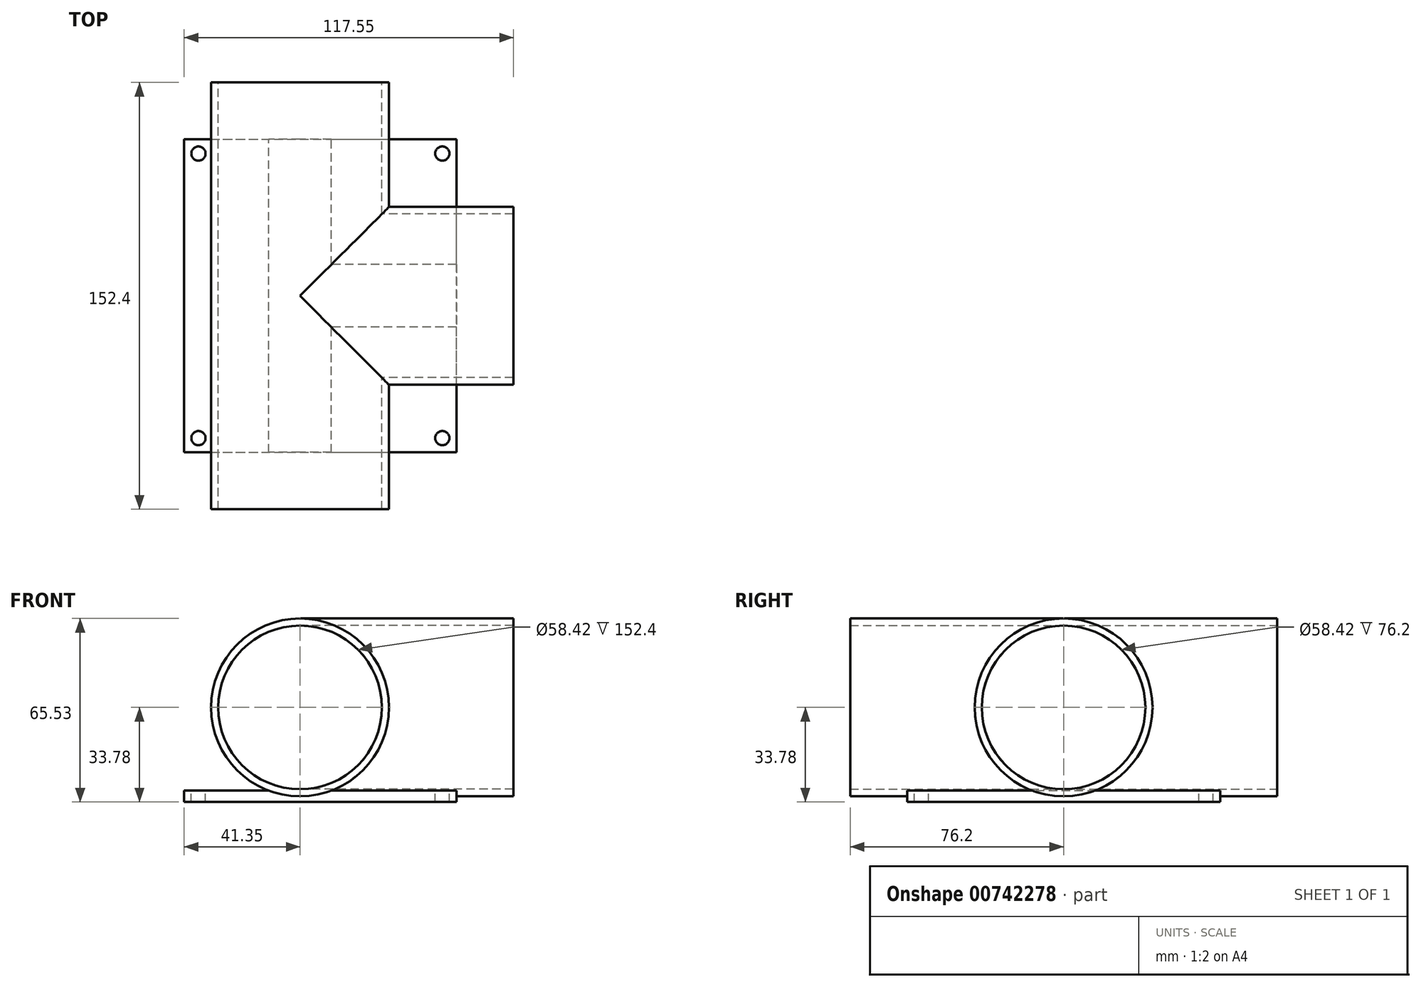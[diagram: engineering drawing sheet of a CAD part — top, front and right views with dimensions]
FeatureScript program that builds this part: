
annotation { "Feature Type Name" : "Feature", "Feature Type Description" : "" }
export const myFeature = defineFeature(function(context is Context, id is Id, definition is map)
    precondition{}
    {
        {
            var Q0;
            Q0=qCreatedBy(makeId("Front.planeOp"),FACE);
            var sketch = newSketch(context, id + "F0", { "sketchPlane" : qUnion([Q0])});
            skCircle(sketch, "E0", {"center": v(0, 0) * mm, "radius": 31.75 * mm});
            skCircle(sketch, "E1.0", {"center": v(0, 0) * mm, "radius": 29.21 * mm});
            skSolve(sketch);
        }
        {
            var Q0;
            Q0=makeQuery(id+"F0.imprint","IMPRINT",FACE,{"disambiguationData":[TD([[makeQuery(id+"F0.imprint","IMPRINT",EDGE,{"derivedFrom":sQuery(id+"F0.wireOp",EDGE,"E0")}),1.0]])]});
            extrude(context, id + "F1", {"entities" : qUnion([Q0]), "endBound" : BoundingType.SYMMETRIC, "depth" : 152.4 * mm, "offsetDistance" : 25.4 * mm});
        }
        {
            var Q0;
            Q0=qCreatedBy(makeId("Right.planeOp"),FACE);
            var sketch = newSketch(context, id + "F2", { "sketchPlane" : qUnion([Q0])});
            skCircle(sketch, "E2", {"center": v(0, 0) * mm, "radius": 31.75 * mm});
            skCircle(sketch, "E3.0", {"center": v(0, 0) * mm, "radius": 29.21 * mm});
            skSolve(sketch);
        }
        {
            var Q0;
            Q0=makeQuery(id+"F2.imprint","IMPRINT",FACE,{"disambiguationData":[TD([[makeQuery(id+"F2.imprint","IMPRINT",EDGE,{"derivedFrom":sQuery(id+"F2.wireOp",EDGE,"E2")}),1.0]])]});
            extrude(context, id + "F3", {"entities" : qUnion([Q0]), "operationType" : NewBodyOperationType.ADD, "depth" : 76.2 * mm, "offsetDistance" : 25.4 * mm});
        }
        {
            var Q0;
            Q0=makeQuery(id+"F0.imprint","IMPRINT",FACE,{"disambiguationData":[TD([[makeQuery(id+"F0.imprint","IMPRINT",EDGE,{"derivedFrom":sQuery(id+"F0.wireOp",EDGE,"E1.0")}),1.0]])]});
            extrude(context, id + "F4", {"entities" : qUnion([Q0]), "operationType" : NewBodyOperationType.REMOVE, "endBound" : BoundingType.SYMMETRIC, "oppositeDirection" : true, "depth" : 105.66 * mm, "offsetDistance" : 25.4 * mm});
        }
        {
            var Q0;
            Q0=makeQuery(id+"F2.imprint","IMPRINT",FACE,{"disambiguationData":[TD([[makeQuery(id+"F2.imprint","IMPRINT",EDGE,{"derivedFrom":sQuery(id+"F2.wireOp",EDGE,"E3.0")}),1.0]])]});
            extrude(context, id + "F5", {"entities" : qUnion([Q0]), "operationType" : NewBodyOperationType.REMOVE, "depth" : 44.45 * mm, "offsetDistance" : 25.4 * mm});
        }
        {
            var Q0;
            Q0=qCreatedBy(makeId("Top.planeOp"),FACE);
            cPlane(context, id + "F6", {"entities" : qUnion([Q0]), "cplaneType" : CPlaneType.OFFSET, "offset" : 31.75 * mm, "oppositeDirection" : true, "width" : 152.4 * mm, "height" : 152.4 * mm});
        }
        {
            var Q0;
            Q0=qCreatedBy(id+"F6.planeOp",FACE);
            var sketch = newSketch(context, id + "F7", { "sketchPlane" : qUnion([Q0])});
            skLineSegment(sketch, "E4.bottom", {"start": v(-41.35, -55.88) * mm, "end": v(55.88, -55.88) * mm});
            skLineSegment(sketch, "E4.top", {"start": v(-41.35, 55.88) * mm, "end": v(55.88, 55.88) * mm});
            skLineSegment(sketch, "E4.left", {"start": v(-41.35, -55.88) * mm, "end": v(-41.35, 55.88) * mm});
            skLineSegment(sketch, "E4.right", {"start": v(55.88, -55.88) * mm, "end": v(55.88, 55.88) * mm});
            skSolve(sketch);
        }
        {
            var Q0;
            Q0=makeQuery(id+"F7.imprint","IMPRINT",FACE,{"disambiguationData":[TD([[makeQuery(id+"F7.imprint","IMPRINT",EDGE,{"derivedFrom":sQuery(id+"F7.wireOp",EDGE,"E4.bottom")}),1.0]])]});
            extrude(context, id + "F8", {"entities" : qUnion([Q0]), "operationType" : NewBodyOperationType.ADD, "endBound" : BoundingType.SYMMETRIC, "depth" : 4.06 * mm, "offsetDistance" : 25.4 * mm});
        }
        {
            var Q0;
            {var subQ0=sQuery(id+"F7.wireOp",EDGE,"E4.top");var subQ1=sQuery(id+"F7.wireOp",EDGE,"E4.bottom");var subQ2=sQuery(id+"F7.wireOp",EDGE,"E4.left");Q0=makeQuery(id+"F8.boolean.opBoolean","SPLIT",FACE,{"disambiguationData":[TD([makeQuery(id+"F1.opExtrude","SWEPT_FACE",FACE,{"disambiguationData":[OSD([sQuery(id+"F0.wireOp",EDGE,"E0")])]}),makeQuery(id+"F8.opExtrude","SWEPT_FACE",FACE,{"disambiguationData":[OSD([subQ1])]}),makeQuery(id+"F8.opExtrude","SWEPT_FACE",FACE,{"disambiguationData":[OSD([subQ0])]}),makeQuery(id+"F8.opExtrude","SWEPT_FACE",FACE,{"disambiguationData":[OSD([subQ2])]})])],"derivedFrom":makeQuery(id+"F8.opExtrude","CAP_FACE",FACE,{"disambiguationData":[OSD([subQ1,subQ0,subQ2,sQuery(id+"F7.wireOp",EDGE,"E4.right")])],"isStart":false})});}
            var sketch = newSketch(context, id + "F9", { "sketchPlane" : qUnion([Q0])});
            skCircle(sketch, "E5", {"center": v(-36.27, 50.8) * mm, "radius": 2.54 * mm});
            skCircle(sketch, "E6", {"center": v(-36.27, -50.8) * mm, "radius": 2.54 * mm});
            skCircle(sketch, "E7", {"center": v(50.8, 50.8) * mm, "radius": 2.54 * mm});
            skCircle(sketch, "E8", {"center": v(50.8, -50.8) * mm, "radius": 2.54 * mm});
            skSolve(sketch);
        }
        {
            var Q0;
            Q0=makeQuery(id+"F9.imprint","IMPRINT",FACE,{"disambiguationData":[TD([[makeQuery(id+"F9.imprint","IMPRINT",EDGE,{"derivedFrom":sQuery(id+"F9.wireOp",EDGE,"E5")}),1.0]])]});
            var Q1;
            Q1=makeQuery(id+"F9.imprint","IMPRINT",FACE,{"disambiguationData":[TD([[makeQuery(id+"F9.imprint","IMPRINT",EDGE,{"derivedFrom":sQuery(id+"F9.wireOp",EDGE,"E7")}),1.0]])]});
            var Q2;
            Q2=makeQuery(id+"F9.imprint","IMPRINT",FACE,{"disambiguationData":[TD([[makeQuery(id+"F9.imprint","IMPRINT",EDGE,{"derivedFrom":sQuery(id+"F9.wireOp",EDGE,"E8")}),1.0]])]});
            var Q3;
            Q3=makeQuery(id+"F9.imprint","IMPRINT",FACE,{"disambiguationData":[TD([[makeQuery(id+"F9.imprint","IMPRINT",EDGE,{"derivedFrom":sQuery(id+"F9.wireOp",EDGE,"E6")}),1.0]])]});
            extrude(context, id + "F10", {"entities" : qUnion([Q0, Q1, Q2, Q3]), "operationType" : NewBodyOperationType.REMOVE, "oppositeDirection" : true, "depth" : 25.4 * mm, "offsetDistance" : 25.4 * mm});
        }
    });
